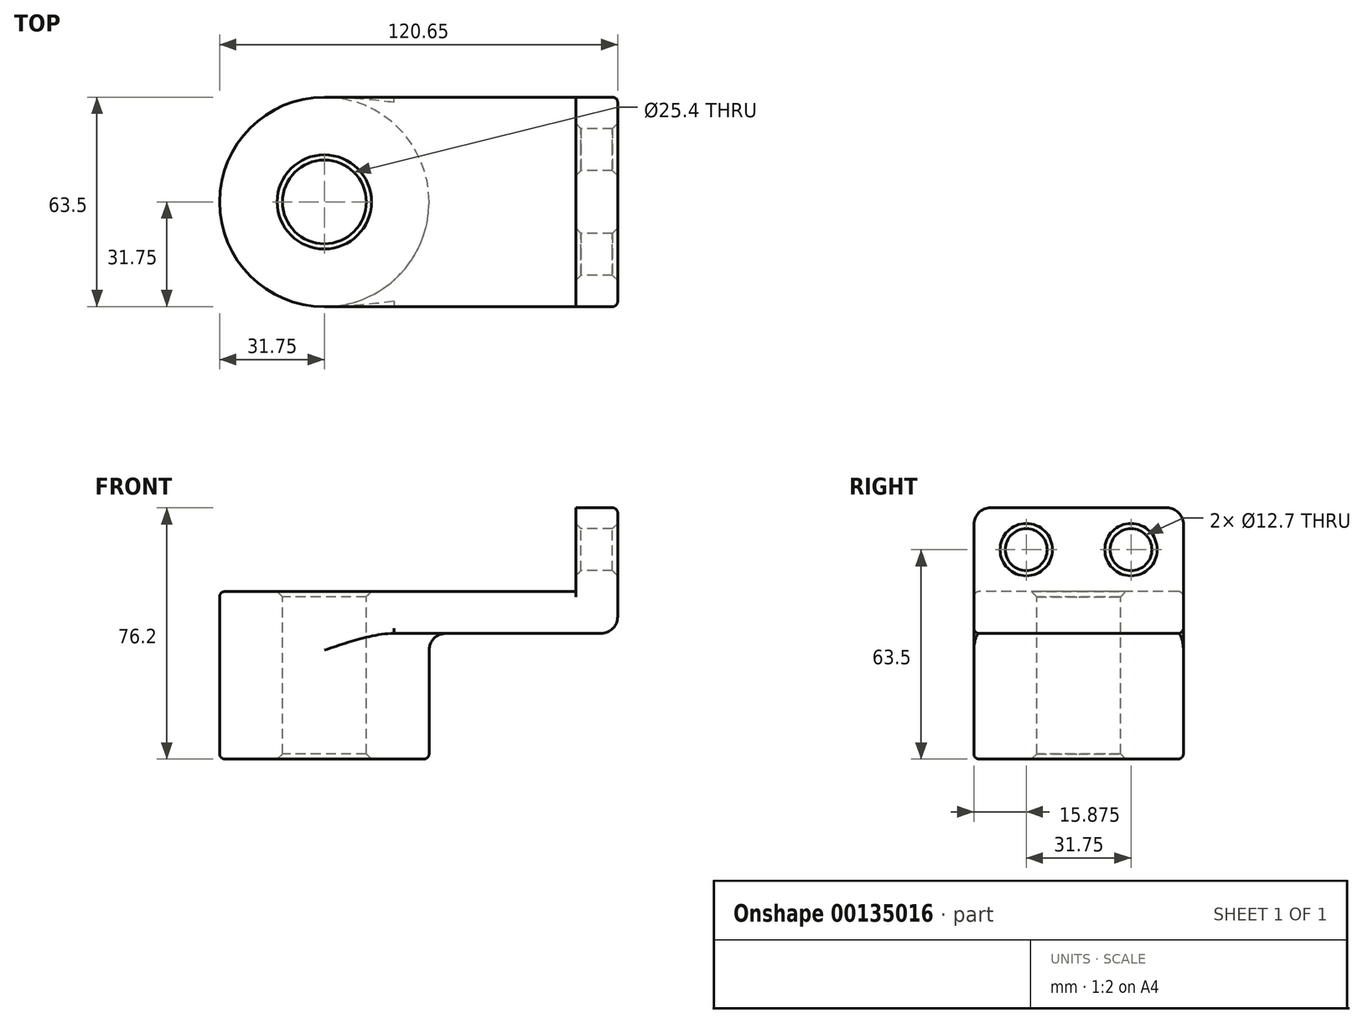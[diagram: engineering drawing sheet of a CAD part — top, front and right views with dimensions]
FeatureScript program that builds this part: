
annotation { "Feature Type Name" : "Feature", "Feature Type Description" : "" }
export const myFeature = defineFeature(function(context is Context, id is Id, definition is map)
    precondition{}
    {
        {
            var Q0;
            Q0=qCreatedBy(makeId("Top.planeOp"),FACE);
            var sketch = newSketch(context, id + "F7", { "sketchPlane" : qUnion([Q0])});
            skLineSegment(sketch, "E0.bottom", {"start": v(38.1, 31.75) * mm, "end": v(-38.1, 31.75) * mm});
            skLineSegment(sketch, "E0.top", {"start": v(38.1, -31.75) * mm, "end": v(-38.1, -31.75) * mm});
            skLineSegment(sketch, "E0.left", {"start": v(38.1, 31.75) * mm, "end": v(38.1, -31.75) * mm});
            skLineSegment(sketch, "E0.right", {"start": v(-38.1, 31.75) * mm, "end": v(-38.1, -31.75) * mm});
            skPoint(sketch, "E0.middle", {"position": v(0, 0) * mm});
            skCircle(sketch, "E1", {"center": v(-38.1, 0) * mm, "radius": 31.75 * mm});
            skCircle(sketch, "E2", {"center": v(-38.1, 0) * mm, "radius": 12.7 * mm});
            skSolve(sketch);
        }
        {
            var Q0;
            Q0 = qSketchRegion(id + "F7", true);
            var Q1;
            {var subQ0=sQuery(id+"F7.wireOp",EDGE,"E0.bottom");Q1=makeQuery(id+"F7.imprint","IMPRINT",FACE,{"disambiguationData":[TD([[makeQuery(id+"F7.imprint","IMPRINT",EDGE,{"derivedFrom":subQ0}),1.0]])]});}
            var Q2;
            {var subQ1=sQuery(id+"F7.wireOp",EDGE,"E0.right");var subQ3=sQuery(id+"F7.wireOp",EDGE,"E2");var subQ4=makeQuery(id+"F7.imprint","INTERSECT",VERTEX,{"disambiguationData":[OD(0.0)],"derivedFrom":[subQ1,subQ3]});Q2=makeQuery(id+"F7.imprint","IMPRINT",FACE,{"disambiguationData":[TD([[makeQuery(id+"F7.imprint","IMPRINT",EDGE,{"disambiguationData":[TD([[subQ4,1.0]])],"derivedFrom":subQ3}),-1.0]])]});}
            var Q3;
            {var subQ1=sQuery(id+"F7.wireOp",EDGE,"E0.right");var subQ3=sQuery(id+"F7.wireOp",EDGE,"E2");var subQ4=makeQuery(id+"F7.imprint","INTERSECT",VERTEX,{"disambiguationData":[OD(0.0)],"derivedFrom":[subQ1,subQ3]});Q3=makeQuery(id+"F7.imprint","IMPRINT",FACE,{"disambiguationData":[TD([[makeQuery(id+"F7.imprint","IMPRINT",EDGE,{"disambiguationData":[TD([[subQ4,-1.0]])],"derivedFrom":subQ3}),-1.0]])]});}
            extrude(context, id + "F0", {"entities" : qUnion([Q0, Q1, Q2, Q3]), "oppositeDirection" : true, "depth" : 12.7 * mm});
        }
        {
            var Q0;
            {var subQ1=sQuery(id+"F7.wireOp",EDGE,"E0.right");var subQ3=sQuery(id+"F7.wireOp",EDGE,"E2");var subQ4=makeQuery(id+"F7.imprint","INTERSECT",VERTEX,{"disambiguationData":[OD(0.0)],"derivedFrom":[subQ1,subQ3]});Q0=makeQuery(id+"F7.imprint","IMPRINT",FACE,{"disambiguationData":[TD([[makeQuery(id+"F7.imprint","IMPRINT",EDGE,{"disambiguationData":[TD([[subQ4,1.0]])],"derivedFrom":subQ3}),-1.0]])]});}
            var Q1;
            {var subQ1=sQuery(id+"F7.wireOp",EDGE,"E0.right");var subQ3=sQuery(id+"F7.wireOp",EDGE,"E2");var subQ4=makeQuery(id+"F7.imprint","INTERSECT",VERTEX,{"disambiguationData":[OD(0.0)],"derivedFrom":[subQ1,subQ3]});Q1=makeQuery(id+"F7.imprint","IMPRINT",FACE,{"disambiguationData":[TD([[makeQuery(id+"F7.imprint","IMPRINT",EDGE,{"disambiguationData":[TD([[subQ4,-1.0]])],"derivedFrom":subQ3}),-1.0]])]});}
            extrude(context, id + "F1", {"entities" : qUnion([Q0, Q1]), "operationType" : NewBodyOperationType.ADD, "oppositeDirection" : true, "depth" : 50.8 * mm});
        }
        {
            var Q0;
            Q0=makeQuery(id+"F0.opExtrude","SWEPT_FACE",FACE,{"disambiguationData":[OSD([sQuery(id+"F7.wireOp",EDGE,"E0.left")])]});
            var sketch = newSketch(context, id + "F2", { "sketchPlane" : qUnion([Q0])});
            skLineSegment(sketch, "E3.bottom", {"start": v(31.75, -12.7) * mm, "end": v(-31.75, -12.7) * mm});
            skLineSegment(sketch, "E3.top", {"start": v(31.75, 25.4) * mm, "end": v(-31.75, 25.4) * mm});
            skLineSegment(sketch, "E3.left", {"start": v(31.75, -12.7) * mm, "end": v(31.75, 25.4) * mm});
            skLineSegment(sketch, "E3.right", {"start": v(-31.75, -12.7) * mm, "end": v(-31.75, 25.4) * mm});
            skLineSegment(sketch, "E4", {"start": v(0, 25.4) * mm, "end": v(0, 0) * mm, "construction": true});
            skCircle(sketch, "E5", {"center": v(15.88, 12.7) * mm, "radius": 6.35 * mm});
            skCircle(sketch, "E6.MirrorC", {"center": v(-15.88, 12.7) * mm, "radius": 6.35 * mm});
            skSolve(sketch);
        }
        {
            var Q0;
            {var subQ0=sQuery(id+"F2.wireOp",EDGE,"E3.bottom");Q0=makeQuery(id+"F2.imprint","IMPRINT",FACE,{"disambiguationData":[TD([[makeQuery(id+"F2.imprint","IMPRINT",EDGE,{"derivedFrom":subQ0}),-1.0]])]});}
            var Q1;
            {var subQ2=sQuery(id+"F2.wireOp",EDGE,"E3.top");Q1=makeQuery(id+"F2.imprint","IMPRINT",FACE,{"disambiguationData":[TD([[makeQuery(id+"F2.imprint","IMPRINT",EDGE,{"derivedFrom":subQ2}),1.0]])]});}
            extrude(context, id + "F3", {"entities" : qUnion([Q0, Q1]), "operationType" : NewBodyOperationType.ADD, "depth" : 12.7 * mm});
        }
        {
            var Q0;
            {var subQ0=sQuery(id+"F7.wireOp",EDGE,"E1");Q0=makeQuery(id+"F1.boolean.opBoolean","INTERSECT",EDGE,{"derivedFrom":[makeQuery(id+"F0.opExtrude","CAP_FACE",FACE,{"disambiguationData":[OSD([sQuery(id+"F7.wireOp",EDGE,"E0.bottom"),sQuery(id+"F7.wireOp",EDGE,"E0.top"),sQuery(id+"F7.wireOp",EDGE,"E0.left"),subQ0,sQuery(id+"F7.wireOp",EDGE,"E2")])],"isStart":false}),makeQuery(id+"F1.opExtrude","SWEPT_FACE",FACE,{"disambiguationData":[OSD([subQ0])]})]});}
            var Q1;
            Q1=makeQuery(id+"F3.opExtrude","CAP_EDGE",EDGE,{"disambiguationData":[OSD([sQuery(id+"F2.wireOp",EDGE,"E3.bottom")])],"isStart":false});
            var Q2;
            Q2=makeQuery(id+"F3.opExtrude","SWEPT_EDGE",EDGE,{"disambiguationData":[OSD([sQuery(id+"F2.wireOp",EDGE,"E3.top"),sQuery(id+"F2.wireOp",EDGE,"E3.right")])]});
            var Q3;
            Q3=makeQuery(id+"F3.opExtrude","SWEPT_EDGE",EDGE,{"disambiguationData":[OSD([sQuery(id+"F2.wireOp",EDGE,"E3.top"),sQuery(id+"F2.wireOp",EDGE,"E3.left")])]});
            var Q4;
            Q4=makeQuery(id+"F0.opExtrude","CAP_EDGE",EDGE,{"disambiguationData":[OSD([sQuery(id+"F7.wireOp",EDGE,"E0.left")])],"isStart":true});
            fillet(context, id + "F4", {"entities" : qUnion([Q0, Q1, Q2, Q3, Q4]), "radius" : 5.08 * mm, "tangentPropagation" : true, "allowEdgeOverflow" : false});
        }
        {
            var Q0;
            Q0=makeQuery(id+"F3.boolean.opBoolean","MERGE",EDGE,{"derivedFrom":[makeQuery(id+"F0.opExtrude","CAP_EDGE",EDGE,{"disambiguationData":[OSD([sQuery(id+"F7.wireOp",EDGE,"E0.bottom")])],"isStart":false}),makeQuery(id+"F3.opExtrude","SWEPT_EDGE",EDGE,{"disambiguationData":[OSD([sQuery(id+"F2.wireOp",EDGE,"E3.bottom"),sQuery(id+"F2.wireOp",EDGE,"E3.left")])]})]});
            var Q1;
            Q1=makeQuery(id+"F3.boolean.opBoolean","MERGE",EDGE,{"derivedFrom":[makeQuery(id+"F0.opExtrude","CAP_EDGE",EDGE,{"disambiguationData":[OSD([sQuery(id+"F7.wireOp",EDGE,"E0.top")])],"isStart":false}),makeQuery(id+"F3.opExtrude","SWEPT_EDGE",EDGE,{"disambiguationData":[OSD([sQuery(id+"F2.wireOp",EDGE,"E3.bottom"),sQuery(id+"F2.wireOp",EDGE,"E3.right")])]})]});
            var Q2;
            Q2=makeQuery(id+"F1.opExtrude","CAP_EDGE",EDGE,{"disambiguationData":[OSD([sQuery(id+"F7.wireOp",EDGE,"E1")])],"isStart":false});
            var Q3;
            Q3=makeQuery(id+"F0.opExtrude","CAP_EDGE",EDGE,{"disambiguationData":[OSD([sQuery(id+"F7.wireOp",EDGE,"E0.top")])],"isStart":true});
            fillet(context, id + "F5", {"entities" : qUnion([Q0, Q1, Q2, Q3]), "radius" : 1.59 * mm, "tangentPropagation" : true, "allowEdgeOverflow" : false});
        }
        {
            var Q0;
            Q0=makeQuery(id+"F1.opExtrude","CAP_EDGE",EDGE,{"disambiguationData":[OSD([sQuery(id+"F7.wireOp",EDGE,"E2")])],"isStart":false});
            var Q1;
            Q1=makeQuery(id+"F0.opExtrude","CAP_EDGE",EDGE,{"disambiguationData":[OSD([sQuery(id+"F7.wireOp",EDGE,"E2")])],"isStart":true});
            chamfer(context, id + "F6", {"entities" : qUnion([Q0, Q1]), "width" : 1.59 * mm, "tangentPropagation" : true});
        }
        {
            var Q0;
            Q0=makeQuery(id+"F3.opExtrude","CAP_EDGE",EDGE,{"disambiguationData":[OSD([sQuery(id+"F2.wireOp",EDGE,"E6.MirrorC")])],"isStart":false});
            var Q1;
            Q1=makeQuery(id+"F3.opExtrude","CAP_EDGE",EDGE,{"disambiguationData":[OSD([sQuery(id+"F2.wireOp",EDGE,"E5")])],"isStart":false});
            var Q2;
            Q2=makeQuery(id+"F3.opExtrude","CAP_EDGE",EDGE,{"disambiguationData":[OSD([sQuery(id+"F2.wireOp",EDGE,"E5")])],"isStart":true});
            var Q3;
            Q3=makeQuery(id+"F3.opExtrude","CAP_EDGE",EDGE,{"disambiguationData":[OSD([sQuery(id+"F2.wireOp",EDGE,"E6.MirrorC")])],"isStart":true});
            chamfer(context, id + "F8", {"entities" : qUnion([Q0, Q1, Q2, Q3]), "width" : 1.59 * mm, "tangentPropagation" : true});
        }
    });
